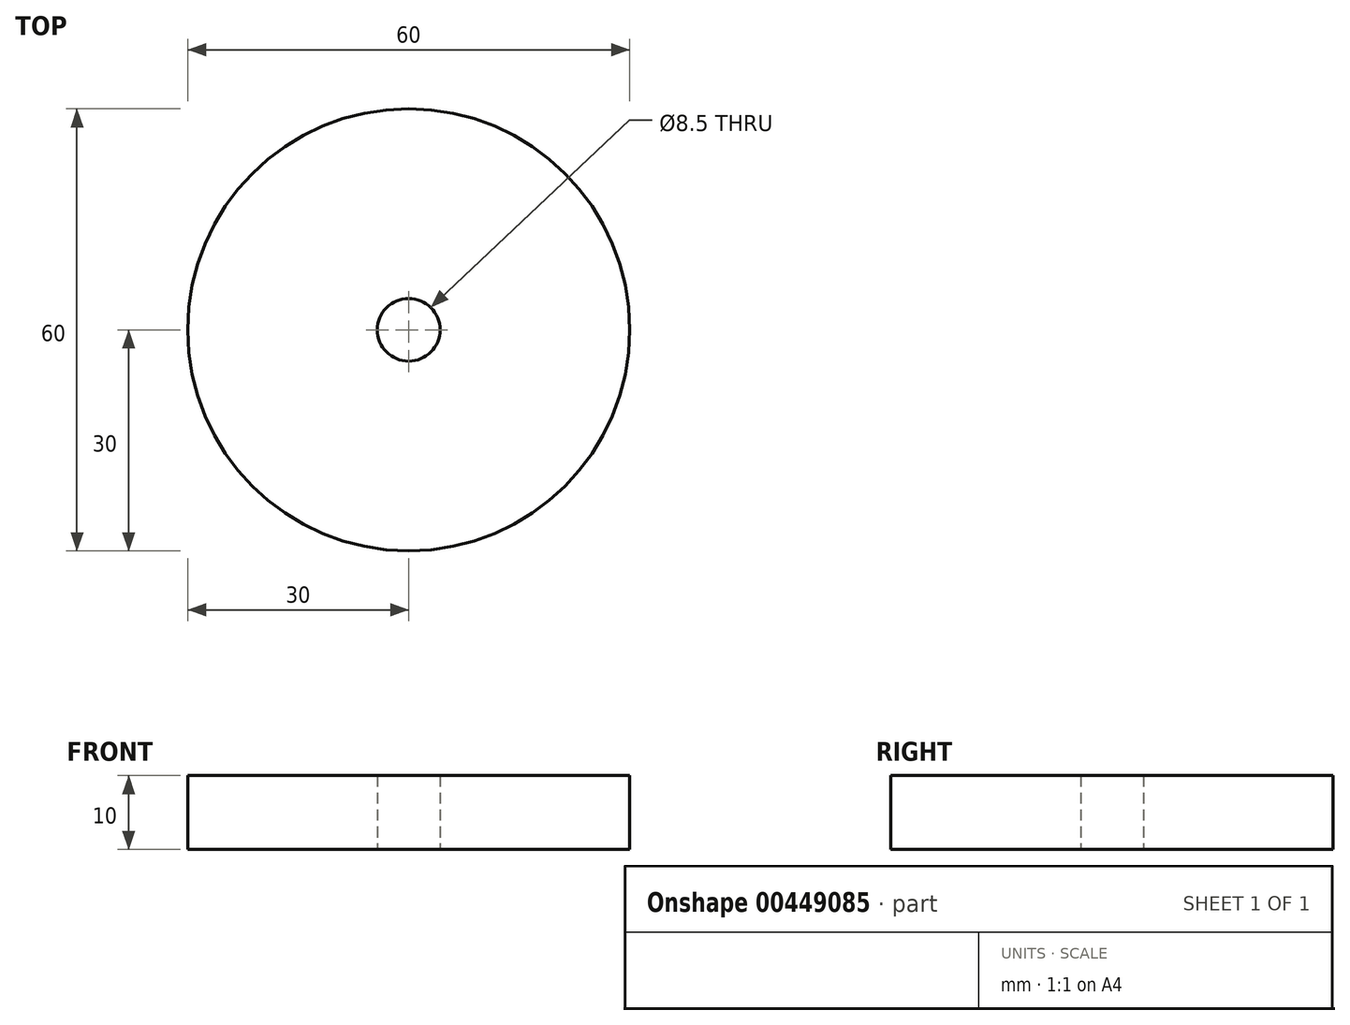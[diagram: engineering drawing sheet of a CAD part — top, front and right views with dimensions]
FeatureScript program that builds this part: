
annotation { "Feature Type Name" : "Feature", "Feature Type Description" : "" }
export const myFeature = defineFeature(function(context is Context, id is Id, definition is map)
    precondition{}
    {
        {
            var Q0;
            Q0=qCreatedBy(makeId("Top.planeOp"),FACE);
            var sketch = newSketch(context, id + "F0", { "sketchPlane" : qUnion([Q0])});
            skCircle(sketch, "E0", {"center": v(0, 0) * mm, "radius": 30 * mm});
            skCircle(sketch, "E1", {"center": v(0, 0) * mm, "radius": 4.25 * mm});
            skSolve(sketch);
        }
        {
            var Q0;
            Q0=makeQuery(id+"F0.imprint","IMPRINT",FACE,{"disambiguationData":[TD([[makeQuery(id+"F0.imprint","IMPRINT",EDGE,{"derivedFrom":sQuery(id+"F0.wireOp",EDGE,"E0")}),1.0]])]});
            extrude(context, id + "F1", {"entities" : qUnion([Q0]), "depth" : 10 * mm});
        }
    });
